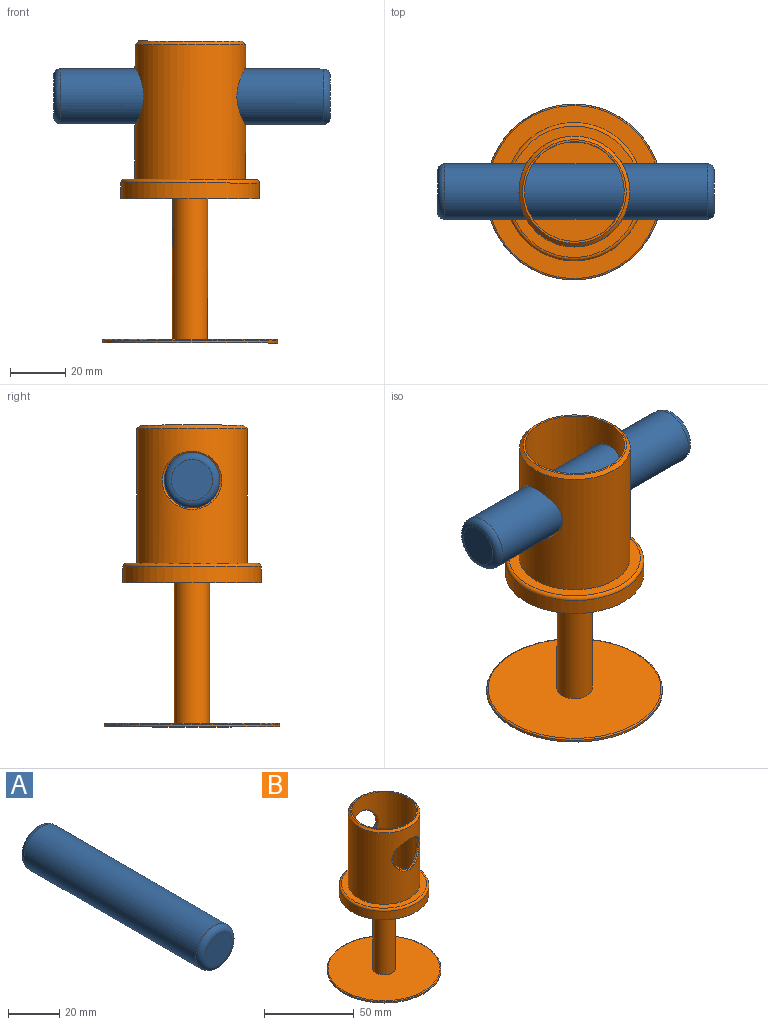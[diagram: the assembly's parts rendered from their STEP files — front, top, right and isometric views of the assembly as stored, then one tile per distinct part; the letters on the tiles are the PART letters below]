
ASSEMBLY  parts=2 mates=1
PART A: 5 faces, bbox 21.6x100x21.6 mm
  f0: cylinder r=10mm len=94.92mm, axis (0,-1,0), area 5964mm2, adj f3,f4
  f1: plane 14.92x14.92mm, normal (0,1,0), area 174.8mm2, adj f4
  f2: plane 14.92x14.92mm, normal (0,-1,0), area 174.8mm2, adj f3
  f3: torus R=7.46mm, axis (0,-1,0), area 227.5mm2, adj f0,f2
  f4: torus R=7.46mm, axis (0,-1,0), area 227.5mm2, adj f0,f1
PART B: 20 faces, bbox 68.7x68.7x109.1 mm
  f0: cylinder r=25mm len=50mm, axis (0,0,1), area 900.1mm2, adj f2,f9
  f1: plane 47.46x47.46mm, normal (0,0,1), area 512.4mm2, adj f4,f9
  f2: plane 50x50mm, normal (0,0,-1), area 1836.8mm2, adj f0,f15
  f3: cylinder r=18mm len=50mm, axis (0,0,1), area 4949.8mm2, adj f5,f6,f11,f12
  f4: cylinder r=20mm len=48.73mm, axis (0,0,1), area 5383.7mm2, adj f1,f10,f13,f14
  f5: plane 37.46x37.46mm, normal (0,0,1), area 84.2mm2, adj f3,f14
  f6: plane 36x36mm, normal (0,0,1), area 1017.9mm2, adj f3
  f7: cylinder r=10mm len=20mm, axis (0,-1,0), area 64.8mm2, adj f10,f11
  f8: cylinder r=10mm len=20mm, axis (0,-1,0), area 74mm2, adj f12,f13
  f9: torus R=23.73mm, axis (0,0,1), area 307.6mm2, adj f0,f1
  f10: bspline ~21.54x21mm, area 52.6mm2, adj f4,f7
  f11: bspline ~21x20.44mm, area 38.8mm2, adj f3,f7
  f12: bspline ~21x20.44mm, area 38.8mm2, adj f3,f8
  f13: bspline ~21.54x21mm, area 52.6mm2, adj f4,f8
  f14: cone r=18.73mm half-angle=45deg, axis (0,0,-1), area 218.5mm2, adj f4,f5
  f15: cylinder r=6.35mm len=50.8mm, axis (0,0,1), area 2026.8mm2, adj f2,f18
  f16: cylinder r=31.75mm len=63.5mm, axis (0,0,1), area 152mm2, adj f17,f19
  f17: plane 63.5x63.5mm, normal (0,0,-1), area 3166.9mm2, adj f16
  f18: plane 62.48x62.48mm, normal (0,0,1), area 2939.7mm2, adj f15,f19
  f19: torus R=31.24mm, axis (0,0,-1), area 158.3mm2, adj f16,f18
PLACE A rot(axis=(0,0,-1),90deg) t=(0.07,24.92,-15.7)mm
PLACE B rot(axis=(0,0,-1),90deg) t=(-0.61,24.92,-52.7)mm
MATE slider A.f0 <-> B.f7  axis (-1,0,0) through (0.07,24.92,-15.7)mm
